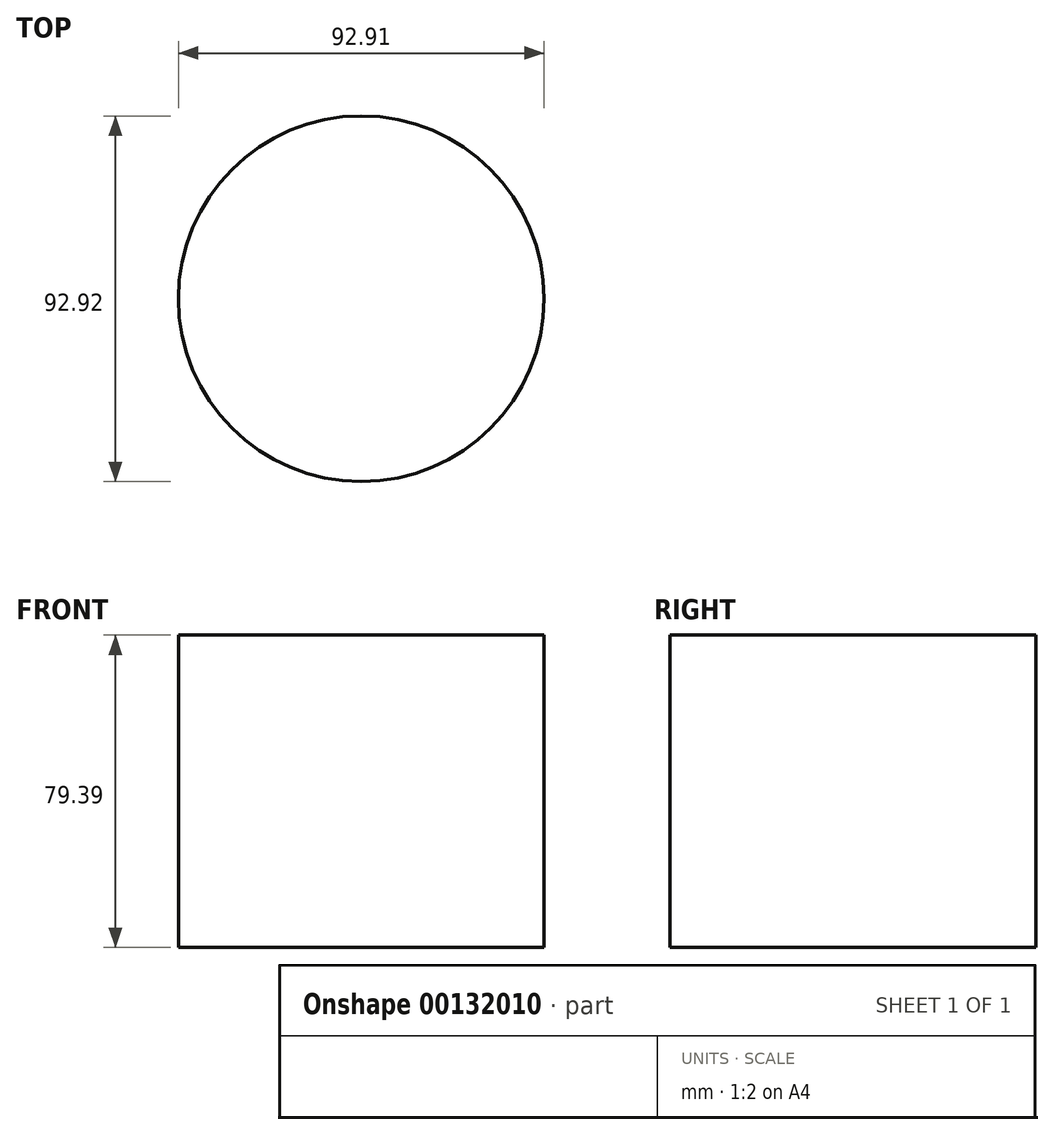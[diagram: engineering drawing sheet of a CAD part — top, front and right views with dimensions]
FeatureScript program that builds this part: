
annotation { "Feature Type Name" : "Feature", "Feature Type Description" : "" }
export const myFeature = defineFeature(function(context is Context, id is Id, definition is map)
    precondition{}
    {
        {
            var Q0;
            Q0=qCreatedBy(makeId("Top.planeOp"),FACE);
            var sketch = newSketch(context, id + "F0", { "sketchPlane" : qUnion([Q0])});
            skCircle(sketch, "E0", {"center": v(8.7, -10.94) * mm, "radius": 46.46 * mm});
            skSolve(sketch);
        }
        {
            var Q0;
            Q0 = qSketchRegion(id + "F0", true);
            extrude(context, id + "F1", {"entities" : qUnion([Q0]), "depth" : 79.39 * mm});
        }
    });
